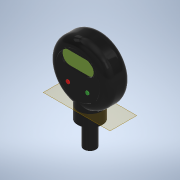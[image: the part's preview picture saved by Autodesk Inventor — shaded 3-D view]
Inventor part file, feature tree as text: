
AUTODESK INVENTOR PART (.ipt)
format: ipt  version: 2021 (Build 250183000, 183)  size: 248,832 bytes
history: native  units: mm
features: extrude x5, sketch x5, other x2, projected_geometry x2, fillet x1
ambient origin geometry x8: Origin, YZ Plane, XZ Plane, XY Plane, X Axis, Y Axis, Z Axis, Center Point
bodies: Body1 (feature_tree)
feature tree (15):
  other  "Bryła1"
  extrude  "Wyciągnięcie proste1"  Depth=50.0mm
  fillet  "Zaokrąglenie1"  Radius=20.0mm
  other  "Płaszczyzna konstrukcyjna1"
  extrude  "Wyciągnięcie proste2"  Depth=7.0mm
  extrude  "Wyciągnięcie proste3"  Depth=10.0mm TaperAngle=0.0deg
  extrude  "Wyciągnięcie proste4"  Depth=10.0mm TaperAngle=0.0deg
  extrude  "Wyciągnięcie proste5"  Depth=10.0mm
  sketch  "Szkic1"
  sketch  "Szkic2"
  sketch  "Szkic3"
  sketch  "Szkic4"
  sketch  "Szkic5"
  projected_geometry  "Pętla rzutowana1"
  projected_geometry  "Pętla rzutowana2"
